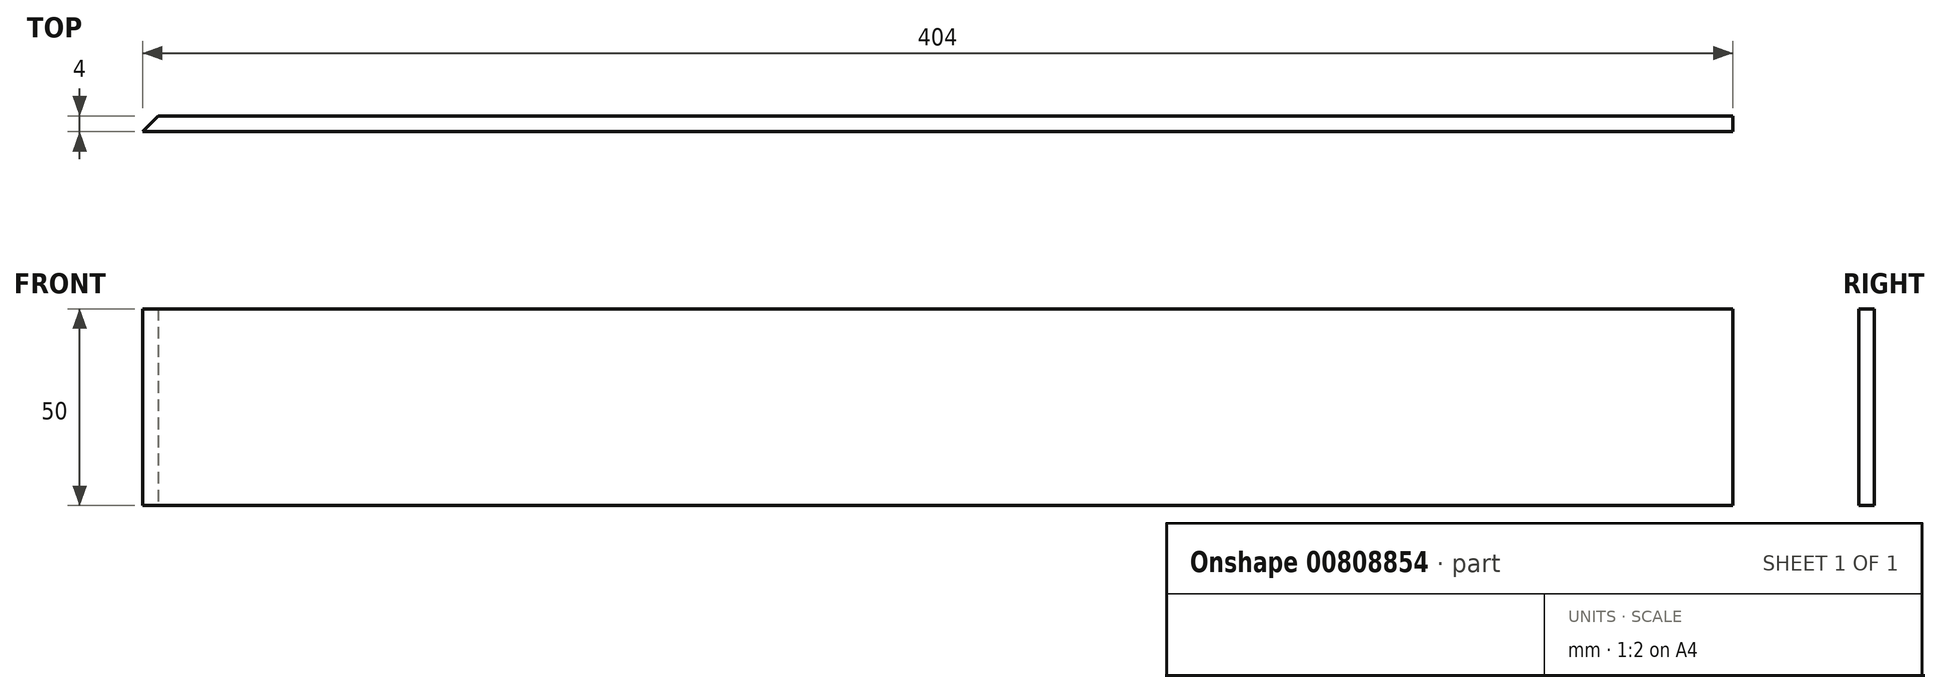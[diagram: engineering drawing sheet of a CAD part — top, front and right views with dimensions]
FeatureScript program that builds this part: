
annotation { "Feature Type Name" : "Feature", "Feature Type Description" : "" }
export const myFeature = defineFeature(function(context is Context, id is Id, definition is map)
    precondition{}
    {
        {
            var Q0;
            Q0=qCreatedBy(makeId("Top.planeOp"),FACE);
            var sketch = newSketch(context, id + "F0", { "sketchPlane" : qUnion([Q0])});
            skLineSegment(sketch, "E0.bottom", {"start": v(0, 0) * mm, "end": v(400, 0) * mm});
            skLineSegment(sketch, "E0.top", {"start": v(0, -4) * mm, "end": v(400, -4) * mm});
            skLineSegment(sketch, "E0.left", {"start": v(0, 0) * mm, "end": v(0, -4) * mm});
            skLineSegment(sketch, "E0.right", {"start": v(400, 0) * mm, "end": v(400, -4) * mm});
            skLineSegment(sketch, "E1", {"start": v(0, -4) * mm, "end": v(-4, -4) * mm});
            skLineSegment(sketch, "E2", {"start": v(-4, -4) * mm, "end": v(0, 0) * mm});
            skSolve(sketch);
        }
        {
            var Q0;
            Q0=makeQuery(id+"F0.imprint","IMPRINT",FACE,{"disambiguationData":[TD([[makeQuery(id+"F0.imprint","IMPRINT",EDGE,{"derivedFrom":sQuery(id+"F0.wireOp",EDGE,"E0.bottom")}),-1.0]])]});
            var Q1;
            Q1=makeQuery(id+"F0.imprint","IMPRINT",FACE,{"disambiguationData":[TD([[makeQuery(id+"F0.imprint","IMPRINT",EDGE,{"derivedFrom":sQuery(id+"F0.wireOp",EDGE,"E0.left")}),-1.0]])]});
            extrude(context, id + "F1", {"entities" : qUnion([Q0, Q1]), "depth" : 50 * mm, "offsetDistance" : 25 * mm});
        }
    });
